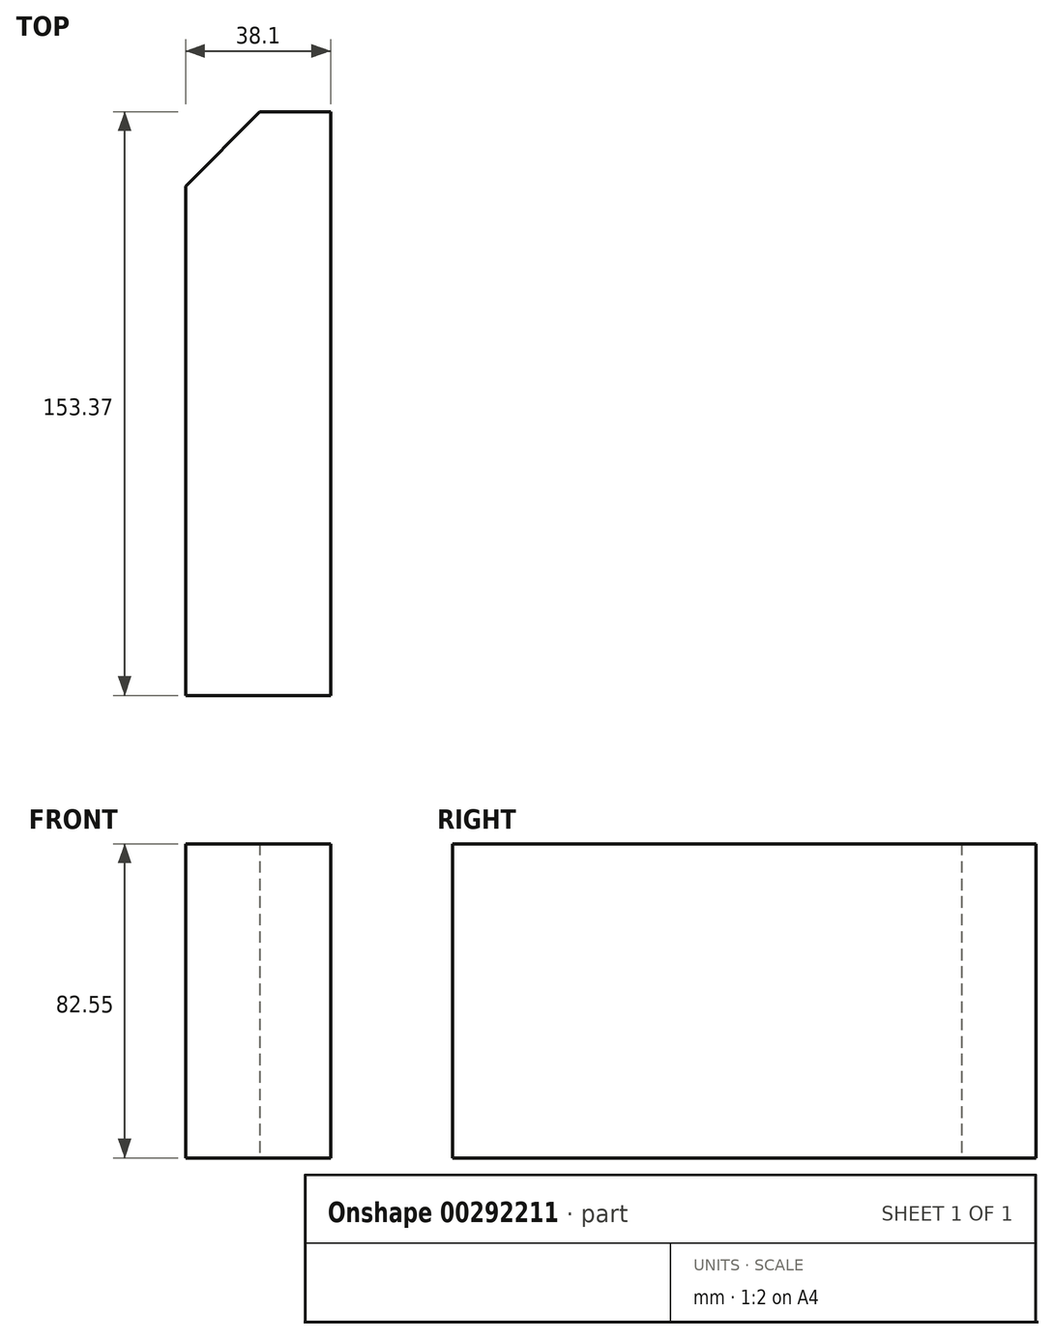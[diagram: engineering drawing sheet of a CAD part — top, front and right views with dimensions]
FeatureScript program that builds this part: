
annotation { "Feature Type Name" : "Feature", "Feature Type Description" : "" }
export const myFeature = defineFeature(function(context is Context, id is Id, definition is map)
    precondition{}
    {
        {
            var Q0;
            Q0=qCreatedBy(makeId("Top.planeOp"),FACE);
            var sketch = newSketch(context, id + "F0", { "sketchPlane" : qUnion([Q0])});
            skLineSegment(sketch, "E0", {"start": v(0, 0) * mm, "end": v(38.1, 0) * mm});
            skLineSegment(sketch, "E1", {"start": v(38.1, 0) * mm, "end": v(38.1, 153.37) * mm});
            skLineSegment(sketch, "E2", {"start": v(38.1, 153.37) * mm, "end": v(19.53, 153.37) * mm});
            skLineSegment(sketch, "E3", {"start": v(0, 133.84) * mm, "end": v(0, 0) * mm});
            skLineSegment(sketch, "E4", {"start": v(0, 133.84) * mm, "end": v(19.53, 153.37) * mm});
            skSolve(sketch);
        }
        {
            var Q0;
            Q0=makeQuery(id+"F0.imprint","IMPRINT",FACE,{"disambiguationData":[TD([[makeQuery(id+"F0.imprint","IMPRINT",EDGE,{"derivedFrom":sQuery(id+"F0.wireOp",EDGE,"E0")}),1.0]])]});
            extrude(context, id + "F1", {"entities" : qUnion([Q0]), "depth" : 82.55 * mm});
        }
    });
